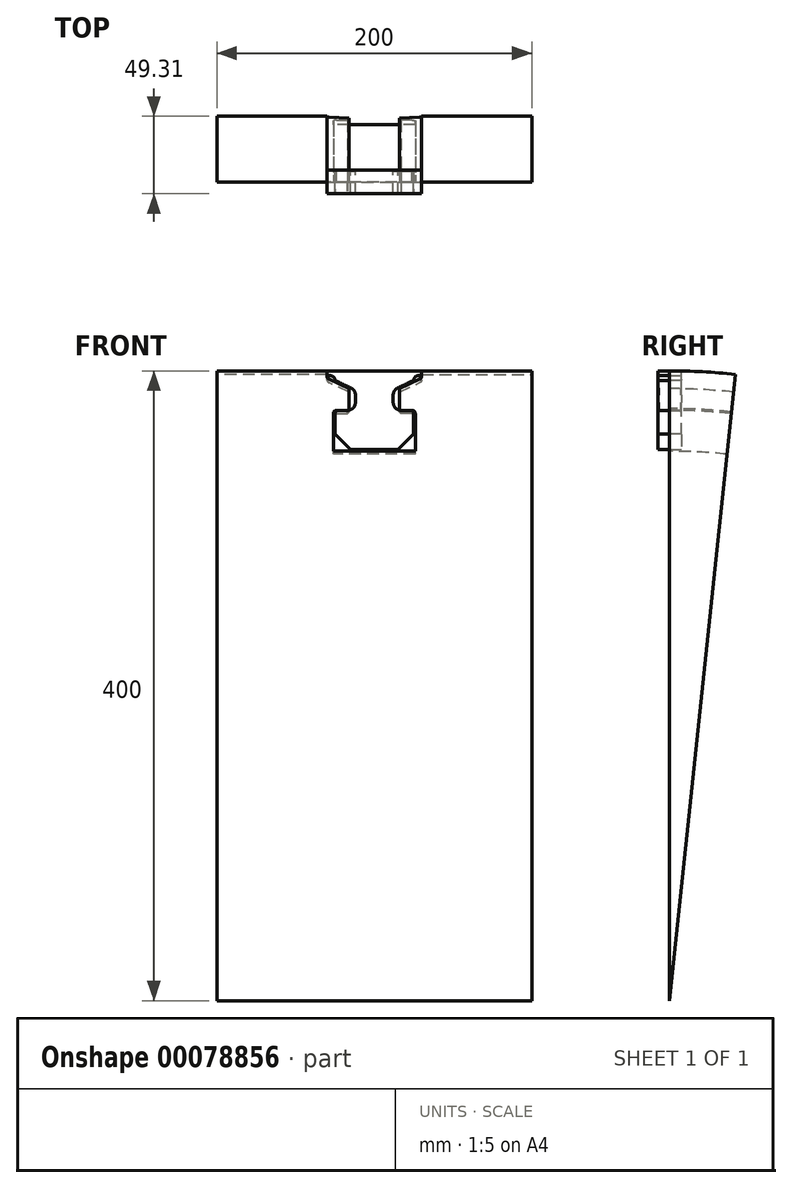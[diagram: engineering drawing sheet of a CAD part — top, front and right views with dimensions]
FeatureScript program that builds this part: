
annotation { "Feature Type Name" : "Feature", "Feature Type Description" : "" }
export const myFeature = defineFeature(function(context is Context, id is Id, definition is map)
    precondition{}
    {
        {
            var Q0;
            Q0=qCreatedBy(makeId("Front.planeOp"),FACE);
            var sketch = newSketch(context, id + "F0", { "sketchPlane" : qUnion([Q0])});
            skLineSegment(sketch, "E0", {"start": v(0, 0) * mm, "end": v(-25, 0) * mm});
            skLineSegment(sketch, "E1", {"start": v(-25, 0) * mm, "end": v(-25, 25) * mm});
            skLineSegment(sketch, "E2", {"start": v(-25, 25) * mm, "end": v(-12, 25) * mm});
            skLineSegment(sketch, "E3", {"start": v(-12, 25) * mm, "end": v(-12, 37.94) * mm});
            skLineSegment(sketch, "E4", {"start": v(-12, 37.94) * mm, "end": v(-25, 44) * mm});
            skLineSegment(sketch, "E5", {"start": v(-30, 50) * mm, "end": v(0, 50) * mm});
            skLineSegment(sketch, "E6", {"start": v(0, 50) * mm, "end": v(0, 0) * mm});
            skLineSegment(sketch, "E7", {"start": v(-25, 47) * mm, "end": v(-30, 47) * mm});
            skLineSegment(sketch, "E8", {"start": v(-30, 47) * mm, "end": v(-30, 50) * mm});
            skLineSegment(sketch, "E9", {"start": v(-25, 44) * mm, "end": v(-25, 47) * mm});
            skLineSegment(sketch, "E10", {"start": v(0, -350) * mm, "end": v(-25, -350) * mm, "construction": true});
            skLineSegment(sketch, "E11", {"start": v(-25, 44) * mm, "end": v(-25, 25) * mm});
            skSolve(sketch);
        }
        {
            var Q0;
            Q0=makeQuery(id+"F0.imprint","IMPRINT",FACE,{"disambiguationData":[TD([[makeQuery(id+"F0.imprint","IMPRINT",EDGE,{"derivedFrom":sQuery(id+"F0.wireOp",EDGE,"E0")}),-1.0]])]});
            var Q1;
            Q1=makeQuery(id+"F0.imprint","IMPRINT",FACE,{"disambiguationData":[TD([[makeQuery(id+"F0.imprint","IMPRINT",EDGE,{"derivedFrom":sQuery(id+"F0.wireOp",EDGE,"E2")}),1.0]])]});
            extrude(context, id + "F1", {"entities" : qUnion([Q0, Q1]), "endBound" : BoundingType.SYMMETRIC, "depth" : 15 * mm});
        }
        {
            var Q0;
            Q0=makeQuery(id+"F0.imprint","IMPRINT",FACE,{"disambiguationData":[TD([[makeQuery(id+"F0.imprint","IMPRINT",EDGE,{"derivedFrom":sQuery(id+"F0.wireOp",EDGE,"E2")}),1.0]])]});
            var Q1;
            Q1=sQuery(id+"F0.wireOp",EDGE,"E10");
            revolve(context, id + "F2", {"operationType" : NewBodyOperationType.REMOVE, "entities" : qUnion([Q0]), "axis" : qUnion([Q1]), "revolveType" : RevolveType.FULL, "oppositeDirection" : true});
        }
        {
            var Q0;
            Q0=makeQuery(id+"F2.boolean.opBoolean","COPY",EDGE,{"derivedFrom":makeQuery(id+"F2.opRevolve","SWEPT_EDGE",EDGE,{"disambiguationData":[OSD([sQuery(id+"F0.wireOp",EDGE,"E2"),sQuery(id+"F0.wireOp",EDGE,"E3")])]})});
            fillet(context, id + "F3", {"entities" : qUnion([Q0]), "radius" : 5 * mm, "tangentPropagation" : true, "allowEdgeOverflow" : false});
        }
        {
            var Q0;
            Q0=makeQuery(id+"F2.boolean.opBoolean","COPY",EDGE,{"derivedFrom":makeQuery(id+"F2.opRevolve","SWEPT_EDGE",EDGE,{"disambiguationData":[OSD([sQuery(id+"F0.wireOp",EDGE,"E3"),sQuery(id+"F0.wireOp",EDGE,"E4")])]})});
            fillet(context, id + "F4", {"entities" : qUnion([Q0]), "radius" : 5 * mm, "tangentPropagation" : true, "allowEdgeOverflow" : false});
        }
        {
            var Q0;
            Q0=makeQuery(id+"F1.opExtrude","SWEPT_EDGE",EDGE,{"disambiguationData":[OSD([sQuery(id+"F0.wireOp",EDGE,"E7"),sQuery(id+"F0.wireOp",EDGE,"E9")])]});
            fillet(context, id + "F5", {"entities" : qUnion([Q0]), "radius" : 3 * mm, "tangentPropagation" : true, "allowEdgeOverflow" : false});
        }
        {
            var Q0;
            Q0=makeQuery(id+"F1.opExtrude","SWEPT_EDGE",EDGE,{"disambiguationData":[OSD([sQuery(id+"F0.wireOp",EDGE,"E0"),sQuery(id+"F0.wireOp",EDGE,"E1")])]});
            chamfer(context, id + "F6", {"entities" : qUnion([Q0]), "width" : 10 * mm, "tangentPropagation" : true});
        }
        {
            var Q0;
            Q0=makeQuery(id+"F2.boolean.opBoolean","COPY",EDGE,{"derivedFrom":makeQuery(id+"F2.opRevolve","SWEPT_EDGE",EDGE,{"disambiguationData":[OSD([sQuery(id+"F0.wireOp",EDGE,"E1"),sQuery(id+"F0.wireOp",EDGE,"E2"),sQuery(id+"F0.wireOp",EDGE,"E11")])]})});
            fillet(context, id + "F7", {"entities" : qUnion([Q0]), "radius" : 1 * mm, "tangentPropagation" : true, "allowEdgeOverflow" : false});
        }
        {
            var Q0;
            Q0=makeQuery(id+"F2.boolean.opBoolean","INTERSECT",EDGE,{"derivedFrom":[makeQuery(id+"F1.opExtrude","CAP_FACE",FACE,{"disambiguationData":[OSD([sQuery(id+"F0.wireOp",EDGE,"E0"),sQuery(id+"F0.wireOp",EDGE,"E1"),sQuery(id+"F0.wireOp",EDGE,"E5"),sQuery(id+"F0.wireOp",EDGE,"E6"),sQuery(id+"F0.wireOp",EDGE,"E7"),sQuery(id+"F0.wireOp",EDGE,"E8"),sQuery(id+"F0.wireOp",EDGE,"E9"),sQuery(id+"F0.wireOp",EDGE,"E11")])],"isStart":false}),makeQuery(id+"F2.opRevolve","SWEPT_FACE",FACE,{"disambiguationData":[OSD([sQuery(id+"F0.wireOp",EDGE,"E2")])]})]});
            var Q1;
            Q1=makeQuery(id+"F2.boolean.opBoolean","INTERSECT",EDGE,{"derivedFrom":[makeQuery(id+"F1.opExtrude","CAP_FACE",FACE,{"disambiguationData":[OSD([sQuery(id+"F0.wireOp",EDGE,"E0"),sQuery(id+"F0.wireOp",EDGE,"E1"),sQuery(id+"F0.wireOp",EDGE,"E5"),sQuery(id+"F0.wireOp",EDGE,"E6"),sQuery(id+"F0.wireOp",EDGE,"E7"),sQuery(id+"F0.wireOp",EDGE,"E8"),sQuery(id+"F0.wireOp",EDGE,"E9"),sQuery(id+"F0.wireOp",EDGE,"E11")])],"isStart":true}),makeQuery(id+"F2.opRevolve","SWEPT_FACE",FACE,{"disambiguationData":[OSD([sQuery(id+"F0.wireOp",EDGE,"E2")])]})]});
            fillet(context, id + "F8", {"entities" : qUnion([Q0, Q1]), "radius" : 0.5 * mm, "tangentPropagation" : true, "allowEdgeOverflow" : false});
        }
        {
            var Q0;
            Q0=qCreatedBy(makeId("Front.planeOp"),FACE);
            var sketch = newSketch(context, id + "F9", { "sketchPlane" : qUnion([Q0])});
            skLineSegment(sketch, "E12", {"start": v(-16.95, 25) * mm, "end": v(-17.05, 25) * mm, "construction": true});
            skLineSegment(sketch, "E13", {"start": v(-17, 25) * mm, "end": v(-17, 24.8) * mm, "construction": true});
            skLineSegment(sketch, "E14", {"start": v(-17, 24.8) * mm, "end": v(-17.05, 25) * mm});
            skLineSegment(sketch, "E15", {"start": v(-17, 24.8) * mm, "end": v(-16.95, 25) * mm});
            skLineSegment(sketch, "E16", {"start": v(-16.95, 25) * mm, "end": v(-16.9, 25.2) * mm});
            skLineSegment(sketch, "E17", {"start": v(-17.05, 25) * mm, "end": v(-17.1, 25.2) * mm});
            skLineSegment(sketch, "E18", {"start": v(-17.1, 25.2) * mm, "end": v(-16.9, 25.2) * mm});
            skSolve(sketch);
        }
        {
            var Q0;
            Q0 = qSketchRegion(id + "F9", true);
            extrude(context, id + "F10", {"entities" : qUnion([Q0]), "operationType" : NewBodyOperationType.REMOVE, "endBound" : BoundingType.THROUGH_ALL, "oppositeDirection" : true, "depth" : 25 * mm, "hasSecondDirection" : true, "secondDirectionBound" : SecondDirectionBoundingType.THROUGH_ALL, "secondDirectionOppositeDirection" : false, "secondDirectionDepth" : 25 * mm});
        }
        {
            var Q0;
            Q0=makeQuery(id+"F1.opExtrude","SWEPT_BODY",BODY,{"disambiguationData":[OSD([sQuery(id+"F0.wireOp",EDGE,"E0"),sQuery(id+"F0.wireOp",EDGE,"E1"),sQuery(id+"F0.wireOp",EDGE,"E5"),sQuery(id+"F0.wireOp",EDGE,"E6"),sQuery(id+"F0.wireOp",EDGE,"E7"),sQuery(id+"F0.wireOp",EDGE,"E8"),sQuery(id+"F0.wireOp",EDGE,"E9"),sQuery(id+"F0.wireOp",EDGE,"E11")])]});
            var Q1;
            Q1=qCreatedBy(makeId("Right.planeOp"),FACE);
            mirror(context, id + "F11", {"operationType" : NewBodyOperationType.ADD, "entities" : qUnion([Q0]), "mirrorPlane" : qUnion([Q1])});
        }
        {
            var Q0;
            Q0=qCreatedBy(makeId("Front.planeOp"),FACE);
            var sketch = newSketch(context, id + "F12", { "sketchPlane" : qUnion([Q0])});
            skLineSegment(sketch, "E19", {"start": v(-26, 25) * mm, "end": v(-16, 25) * mm});
            skLineSegment(sketch, "E20", {"start": v(-16, 25) * mm, "end": v(-16, 38.7) * mm});
            skLineSegment(sketch, "E21", {"start": v(-16, 38.7) * mm, "end": v(-30, 45.23) * mm});
            skLineSegment(sketch, "E22", {"start": v(-30, 45.23) * mm, "end": v(-30, 50) * mm});
            skLineSegment(sketch, "E23", {"start": v(-30, 50) * mm, "end": v(-100, 50) * mm});
            skLineSegment(sketch, "E24", {"start": v(-100, 50) * mm, "end": v(-100, -350) * mm});
            skLineSegment(sketch, "E25", {"start": v(-100, -350) * mm, "end": v(0, -350) * mm});
            skLineSegment(sketch, "E26", {"start": v(0, -350) * mm, "end": v(0, -1) * mm});
            skLineSegment(sketch, "E27", {"start": v(0, -1) * mm, "end": v(-26, -1) * mm});
            skLineSegment(sketch, "E28", {"start": v(-26, -1) * mm, "end": v(-26, 25) * mm});
            skSolve(sketch);
        }
        {
            var Q0;
            Q0 = qSketchRegion(id + "F12", true);
            var Q1;
            Q1=sQuery(id+"F12.wireOp",EDGE,"E25");
            revolve(context, id + "F13", {"entities" : qUnion([Q0]), "axis" : qUnion([Q1]), "revolveType" : RevolveType.ONE_DIRECTION, "oppositeDirection" : true, "angle" : 6 * degree});
        }
        {
            var Q0;
            Q0=makeQuery(id+"F13.opRevolve","SWEPT_EDGE",EDGE,{"disambiguationData":[OSD([sQuery(id+"F12.wireOp",EDGE,"E19"),sQuery(id+"F12.wireOp",EDGE,"E20")])]});
            chamfer(context, id + "F14", {"entities" : qUnion([Q0]), "width" : 1 * mm, "tangentPropagation" : true});
        }
        {
            var Q0;
            Q0=makeQuery(id+"F13.opRevolve","SWEPT_EDGE",EDGE,{"disambiguationData":[OSD([sQuery(id+"F12.wireOp",EDGE,"E21"),sQuery(id+"F12.wireOp",EDGE,"E22")])]});
            fillet(context, id + "F15", {"entities" : qUnion([Q0]), "radius" : 2 * mm, "tangentPropagation" : true, "allowEdgeOverflow" : false});
        }
        {
            var Q0;
            Q0=makeQuery(id+"F13.opRevolve","SWEPT_EDGE",EDGE,{"disambiguationData":[OSD([sQuery(id+"F12.wireOp",EDGE,"E19"),sQuery(id+"F12.wireOp",EDGE,"E28")])]});
            fillet(context, id + "F16", {"entities" : qUnion([Q0]), "radius" : 2 * mm, "tangentPropagation" : true, "allowEdgeOverflow" : false});
        }
        {
            var Q0;
            Q0=makeQuery(id+"F13.opRevolve","SWEPT_BODY",BODY,{"disambiguationData":[OSD([sQuery(id+"F12.wireOp",EDGE,"E19"),sQuery(id+"F12.wireOp",EDGE,"E20"),sQuery(id+"F12.wireOp",EDGE,"E21"),sQuery(id+"F12.wireOp",EDGE,"E22"),sQuery(id+"F12.wireOp",EDGE,"E23"),sQuery(id+"F12.wireOp",EDGE,"E24"),sQuery(id+"F12.wireOp",EDGE,"E25"),sQuery(id+"F12.wireOp",EDGE,"E26"),sQuery(id+"F12.wireOp",EDGE,"E27"),sQuery(id+"F12.wireOp",EDGE,"E28")])]});
            var Q1;
            Q1=qCreatedBy(makeId("Right.planeOp"),FACE);
            mirror(context, id + "F17", {"operationType" : NewBodyOperationType.ADD, "entities" : qUnion([Q0]), "mirrorPlane" : qUnion([Q1])});
        }
        {
            var Q0;
            Q0=makeQuery(id+"F10.boolean.opBoolean","COPY",EDGE,{"derivedFrom":makeQuery(id+"F10.opExtrude","SWEPT_EDGE",EDGE,{"disambiguationData":[OSD([sQuery(id+"F9.wireOp",EDGE,"E14"),sQuery(id+"F9.wireOp",EDGE,"E15")])]})});
            fillet(context, id + "F18", {"entities" : qUnion([Q0]), "radius" : 0.06 * mm, "allowEdgeOverflow" : false});
        }
    });
